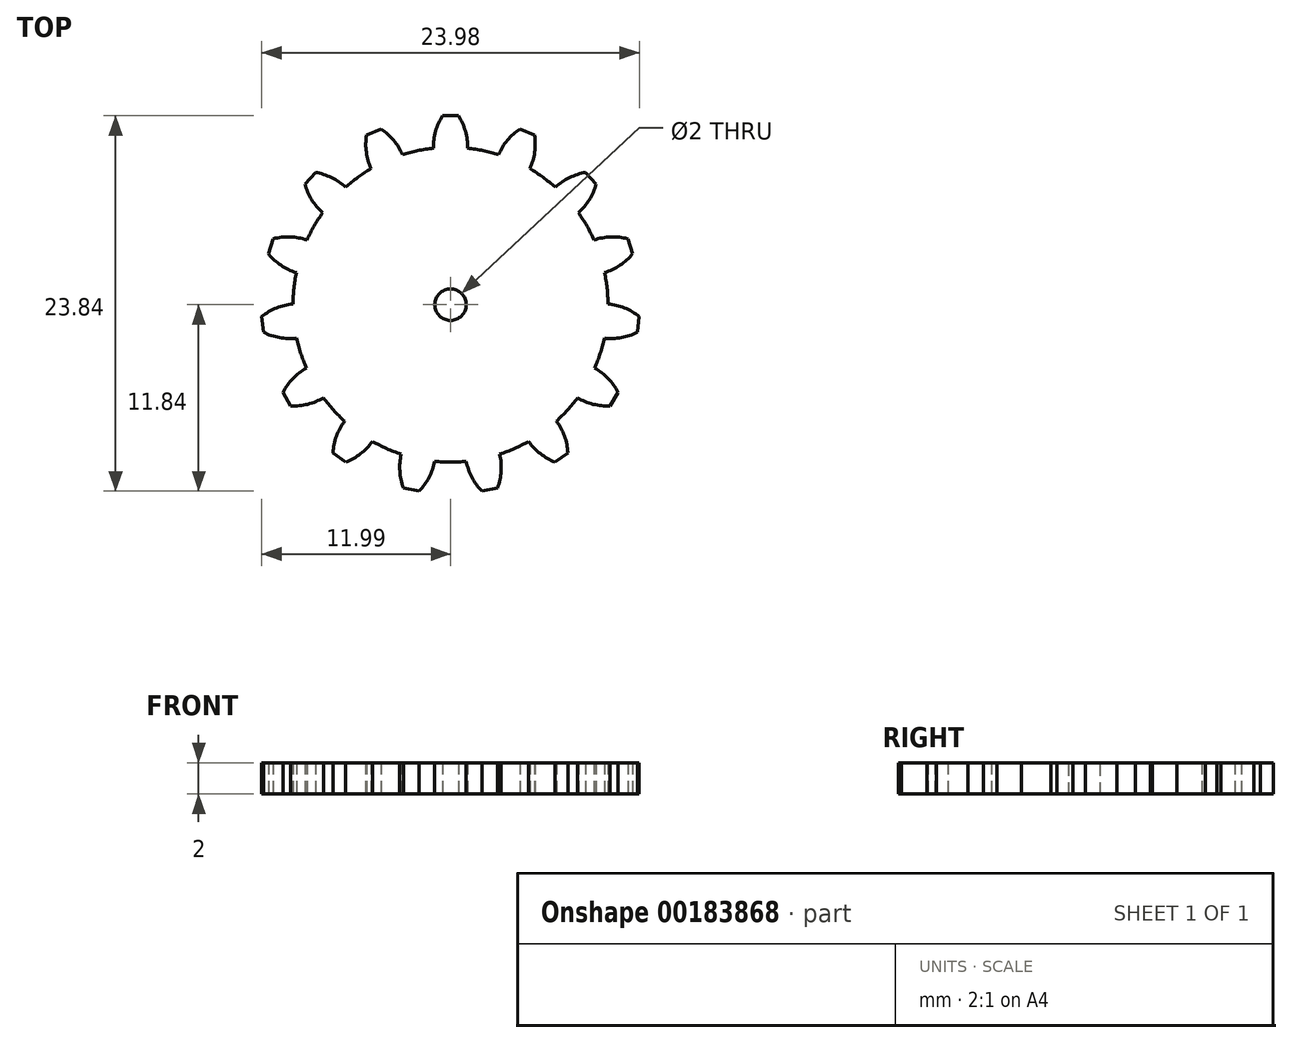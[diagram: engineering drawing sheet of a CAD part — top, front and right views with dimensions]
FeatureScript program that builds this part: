
annotation { "Feature Type Name" : "Feature", "Feature Type Description" : "" }
export const myFeature = defineFeature(function(context is Context, id is Id, definition is map)
    precondition{}
    {
        {
            var Q0;
            Q0=qCreatedBy(makeId("Top.planeOp"),FACE);
            var sketch = newSketch(context, id + "F0", { "sketchPlane" : qUnion([Q0])});
            skCircle(sketch, "E0", {"center": v(0, 0) * mm, "radius": 10 * mm});
            skLineSegment(sketch, "E1", {"start": v(0, 0) * mm, "end": v(0, 10) * mm, "construction": true});
            skLineSegment(sketch, "E2", {"start": v(0, 12) * mm, "end": v(-0.5, 12) * mm});
            skArc(sketch, "E3", {"start": v(-0.5, 12) * mm, "mid": v(-0.95, 11.01) * mm, "end": v(-1.09, 9.94) * mm});
            skLineSegment(sketch, "E4.MirrorCS", {"start": v(0, 12) * mm, "end": v(0.5, 12) * mm});
            skArc(sketch, "E5.MirrorCS", {"start": v(0.5, 12) * mm, "mid": v(0.95, 11.01) * mm, "end": v(1.09, 9.94) * mm});
            skArc(sketch, "E6.1.0", {"start": v(-5.34, 10.76) * mm, "mid": v(-5.34, 9.68) * mm, "end": v(-5.04, 8.64) * mm});
            skLineSegment(sketch, "E6.1.1", {"start": v(-4.88, 10.96) * mm, "end": v(-5.34, 10.76) * mm});
            skLineSegment(sketch, "E6.1.2", {"start": v(-4.88, 10.96) * mm, "end": v(-4.42, 11.17) * mm});
            skArc(sketch, "E6.1.3", {"start": v(-4.42, 11.17) * mm, "mid": v(-3.61, 10.45) * mm, "end": v(-3.05, 9.52) * mm});
            skArc(sketch, "E6.2.0", {"start": v(-9.25, 7.66) * mm, "mid": v(-8.82, 6.67) * mm, "end": v(-8.12, 5.84) * mm});
            skLineSegment(sketch, "E6.2.1", {"start": v(-8.92, 8.03) * mm, "end": v(-9.25, 7.66) * mm});
            skLineSegment(sketch, "E6.2.2", {"start": v(-8.92, 8.03) * mm, "end": v(-8.58, 8.4) * mm});
            skArc(sketch, "E6.2.3", {"start": v(-8.58, 8.4) * mm, "mid": v(-7.55, 8.07) * mm, "end": v(-6.66, 7.46) * mm});
            skArc(sketch, "E6.3.0", {"start": v(-11.57, 3.23) * mm, "mid": v(-10.77, 2.5) * mm, "end": v(-9.8, 2.04) * mm});
            skLineSegment(sketch, "E6.3.1", {"start": v(-11.41, 3.7) * mm, "end": v(-11.57, 3.23) * mm});
            skLineSegment(sketch, "E6.3.2", {"start": v(-11.41, 3.7) * mm, "end": v(-11.26, 4.18) * mm});
            skArc(sketch, "E6.3.3", {"start": v(-11.26, 4.18) * mm, "mid": v(-10.18, 4.3) * mm, "end": v(-9.12, 4.1) * mm});
            skArc(sketch, "E6.4.0", {"start": v(-11.88, -1.75) * mm, "mid": v(-10.85, -2.1) * mm, "end": v(-9.77, -2.12) * mm});
            skLineSegment(sketch, "E6.4.1", {"start": v(-11.93, -1.25) * mm, "end": v(-11.88, -1.75) * mm});
            skLineSegment(sketch, "E6.4.2", {"start": v(-11.93, -1.25) * mm, "end": v(-11.99, -0.76) * mm});
            skArc(sketch, "E6.4.3", {"start": v(-11.99, -0.76) * mm, "mid": v(-11.05, -0.2) * mm, "end": v(-10, 0.04) * mm});
            skArc(sketch, "E6.5.0", {"start": v(-10.14, -6.43) * mm, "mid": v(-9.06, -6.33) * mm, "end": v(-8.06, -5.91) * mm});
            skLineSegment(sketch, "E6.5.1", {"start": v(-10.4, -6) * mm, "end": v(-10.14, -6.43) * mm});
            skLineSegment(sketch, "E6.5.2", {"start": v(-10.4, -6) * mm, "end": v(-10.64, -5.57) * mm});
            skArc(sketch, "E6.5.3", {"start": v(-10.64, -5.57) * mm, "mid": v(-10.01, -4.69) * mm, "end": v(-9.15, -4.03) * mm});
            skArc(sketch, "E6.6.0", {"start": v(-6.65, -10) * mm, "mid": v(-5.7, -9.47) * mm, "end": v(-4.96, -8.68) * mm});
            skLineSegment(sketch, "E6.6.1", {"start": v(-7.05, -9.7) * mm, "end": v(-6.65, -10) * mm});
            skLineSegment(sketch, "E6.6.2", {"start": v(-7.05, -9.7) * mm, "end": v(-7.46, -9.41) * mm});
            skArc(sketch, "E6.6.3", {"start": v(-7.46, -9.41) * mm, "mid": v(-7.24, -8.35) * mm, "end": v(-6.72, -7.4) * mm});
            skArc(sketch, "E6.7.0", {"start": v(-2, -11.84) * mm, "mid": v(-1.36, -10.97) * mm, "end": v(-1, -9.95) * mm});
            skLineSegment(sketch, "E6.7.1", {"start": v(-2.5, -11.74) * mm, "end": v(-2, -11.84) * mm});
            skLineSegment(sketch, "E6.7.2", {"start": v(-2.5, -11.74) * mm, "end": v(-2.98, -11.63) * mm});
            skArc(sketch, "E6.7.3", {"start": v(-2.98, -11.63) * mm, "mid": v(-3.22, -10.58) * mm, "end": v(-3.13, -9.5) * mm});
            skArc(sketch, "E6.8.0", {"start": v(2.98, -11.63) * mm, "mid": v(3.22, -10.58) * mm, "end": v(3.13, -9.5) * mm});
            skLineSegment(sketch, "E6.8.1", {"start": v(2.5, -11.74) * mm, "end": v(2.98, -11.63) * mm});
            skLineSegment(sketch, "E6.8.2", {"start": v(2.5, -11.74) * mm, "end": v(2, -11.84) * mm});
            skArc(sketch, "E6.8.3", {"start": v(2, -11.84) * mm, "mid": v(1.36, -10.97) * mm, "end": v(1, -9.95) * mm});
            skArc(sketch, "E6.9.0", {"start": v(7.46, -9.41) * mm, "mid": v(7.24, -8.35) * mm, "end": v(6.72, -7.4) * mm});
            skLineSegment(sketch, "E6.9.1", {"start": v(7.05, -9.7) * mm, "end": v(7.46, -9.41) * mm});
            skLineSegment(sketch, "E6.9.2", {"start": v(7.05, -9.7) * mm, "end": v(6.65, -10) * mm});
            skArc(sketch, "E6.9.3", {"start": v(6.65, -10) * mm, "mid": v(5.7, -9.47) * mm, "end": v(4.96, -8.68) * mm});
            skArc(sketch, "E6.10.0", {"start": v(10.64, -5.57) * mm, "mid": v(10.01, -4.69) * mm, "end": v(9.15, -4.03) * mm});
            skLineSegment(sketch, "E6.10.1", {"start": v(10.4, -6) * mm, "end": v(10.64, -5.57) * mm});
            skLineSegment(sketch, "E6.10.2", {"start": v(10.4, -6) * mm, "end": v(10.14, -6.43) * mm});
            skArc(sketch, "E6.10.3", {"start": v(10.14, -6.43) * mm, "mid": v(9.06, -6.33) * mm, "end": v(8.06, -5.91) * mm});
            skArc(sketch, "E6.11.0", {"start": v(11.99, -0.76) * mm, "mid": v(11.05, -0.2) * mm, "end": v(10, 0.04) * mm});
            skLineSegment(sketch, "E6.11.1", {"start": v(11.93, -1.25) * mm, "end": v(11.99, -0.76) * mm});
            skLineSegment(sketch, "E6.11.2", {"start": v(11.93, -1.25) * mm, "end": v(11.88, -1.75) * mm});
            skArc(sketch, "E6.11.3", {"start": v(11.88, -1.75) * mm, "mid": v(10.85, -2.1) * mm, "end": v(9.77, -2.12) * mm});
            skArc(sketch, "E6.12.0", {"start": v(11.26, 4.18) * mm, "mid": v(10.18, 4.3) * mm, "end": v(9.12, 4.1) * mm});
            skLineSegment(sketch, "E6.12.1", {"start": v(11.41, 3.7) * mm, "end": v(11.26, 4.18) * mm});
            skLineSegment(sketch, "E6.12.2", {"start": v(11.41, 3.7) * mm, "end": v(11.57, 3.23) * mm});
            skArc(sketch, "E6.12.3", {"start": v(11.57, 3.23) * mm, "mid": v(10.77, 2.5) * mm, "end": v(9.8, 2.04) * mm});
            skArc(sketch, "E6.13.0", {"start": v(8.58, 8.4) * mm, "mid": v(7.55, 8.07) * mm, "end": v(6.66, 7.46) * mm});
            skLineSegment(sketch, "E6.13.1", {"start": v(8.92, 8.03) * mm, "end": v(8.58, 8.4) * mm});
            skLineSegment(sketch, "E6.13.2", {"start": v(8.92, 8.03) * mm, "end": v(9.25, 7.66) * mm});
            skArc(sketch, "E6.13.3", {"start": v(9.25, 7.66) * mm, "mid": v(8.82, 6.67) * mm, "end": v(8.12, 5.84) * mm});
            skArc(sketch, "E6.14.0", {"start": v(4.42, 11.17) * mm, "mid": v(3.61, 10.45) * mm, "end": v(3.05, 9.52) * mm});
            skLineSegment(sketch, "E6.14.1", {"start": v(4.88, 10.96) * mm, "end": v(4.42, 11.17) * mm});
            skLineSegment(sketch, "E6.14.2", {"start": v(4.88, 10.96) * mm, "end": v(5.34, 10.76) * mm});
            skArc(sketch, "E6.14.3", {"start": v(5.34, 10.76) * mm, "mid": v(5.34, 9.68) * mm, "end": v(5.04, 8.64) * mm});
            skSolve(sketch);
        }
        {
            var Q0;
            Q0 = qSketchRegion(id + "F0", true);
            extrude(context, id + "F1", {"entities" : qUnion([Q0]), "depth" : 2 * mm});
        }
        {
            var Q0;
            Q0=makeQuery(id+"F1.opExtrude","CAP_FACE",FACE,{"disambiguationData":[OSD([sQuery(id+"F0.wireOp",EDGE,"E0"),sQuery(id+"F0.wireOp",EDGE,"E2"),sQuery(id+"F0.wireOp",EDGE,"E3"),sQuery(id+"F0.wireOp",EDGE,"E4.MirrorCS"),sQuery(id+"F0.wireOp",EDGE,"E5.MirrorCS"),sQuery(id+"F0.wireOp",EDGE,"E6.1.0"),sQuery(id+"F0.wireOp",EDGE,"E6.1.1"),sQuery(id+"F0.wireOp",EDGE,"E6.1.2"),sQuery(id+"F0.wireOp",EDGE,"E6.1.3"),sQuery(id+"F0.wireOp",EDGE,"E6.2.0"),sQuery(id+"F0.wireOp",EDGE,"E6.2.1"),sQuery(id+"F0.wireOp",EDGE,"E6.2.2"),sQuery(id+"F0.wireOp",EDGE,"E6.2.3"),sQuery(id+"F0.wireOp",EDGE,"E6.3.0"),sQuery(id+"F0.wireOp",EDGE,"E6.3.1"),sQuery(id+"F0.wireOp",EDGE,"E6.3.2"),sQuery(id+"F0.wireOp",EDGE,"E6.3.3"),sQuery(id+"F0.wireOp",EDGE,"E6.4.0"),sQuery(id+"F0.wireOp",EDGE,"E6.4.1"),sQuery(id+"F0.wireOp",EDGE,"E6.4.2"),sQuery(id+"F0.wireOp",EDGE,"E6.4.3"),sQuery(id+"F0.wireOp",EDGE,"E6.5.0"),sQuery(id+"F0.wireOp",EDGE,"E6.5.1"),sQuery(id+"F0.wireOp",EDGE,"E6.5.2"),sQuery(id+"F0.wireOp",EDGE,"E6.5.3"),sQuery(id+"F0.wireOp",EDGE,"E6.6.0"),sQuery(id+"F0.wireOp",EDGE,"E6.6.1"),sQuery(id+"F0.wireOp",EDGE,"E6.6.2"),sQuery(id+"F0.wireOp",EDGE,"E6.6.3"),sQuery(id+"F0.wireOp",EDGE,"E6.7.0"),sQuery(id+"F0.wireOp",EDGE,"E6.7.1"),sQuery(id+"F0.wireOp",EDGE,"E6.7.2"),sQuery(id+"F0.wireOp",EDGE,"E6.7.3"),sQuery(id+"F0.wireOp",EDGE,"E6.8.0"),sQuery(id+"F0.wireOp",EDGE,"E6.8.1"),sQuery(id+"F0.wireOp",EDGE,"E6.8.2"),sQuery(id+"F0.wireOp",EDGE,"E6.8.3"),sQuery(id+"F0.wireOp",EDGE,"E6.9.0"),sQuery(id+"F0.wireOp",EDGE,"E6.9.1"),sQuery(id+"F0.wireOp",EDGE,"E6.9.2"),sQuery(id+"F0.wireOp",EDGE,"E6.9.3"),sQuery(id+"F0.wireOp",EDGE,"E6.10.0"),sQuery(id+"F0.wireOp",EDGE,"E6.10.1"),sQuery(id+"F0.wireOp",EDGE,"E6.10.2"),sQuery(id+"F0.wireOp",EDGE,"E6.10.3"),sQuery(id+"F0.wireOp",EDGE,"E6.11.0"),sQuery(id+"F0.wireOp",EDGE,"E6.11.1"),sQuery(id+"F0.wireOp",EDGE,"E6.11.2"),sQuery(id+"F0.wireOp",EDGE,"E6.11.3"),sQuery(id+"F0.wireOp",EDGE,"E6.12.0"),sQuery(id+"F0.wireOp",EDGE,"E6.12.1"),sQuery(id+"F0.wireOp",EDGE,"E6.12.2"),sQuery(id+"F0.wireOp",EDGE,"E6.12.3"),sQuery(id+"F0.wireOp",EDGE,"E6.13.0"),sQuery(id+"F0.wireOp",EDGE,"E6.13.1"),sQuery(id+"F0.wireOp",EDGE,"E6.13.2"),sQuery(id+"F0.wireOp",EDGE,"E6.13.3"),sQuery(id+"F0.wireOp",EDGE,"E6.14.0"),sQuery(id+"F0.wireOp",EDGE,"E6.14.1"),sQuery(id+"F0.wireOp",EDGE,"E6.14.2"),sQuery(id+"F0.wireOp",EDGE,"E6.14.3")])],"isStart":false});
            var sketch = newSketch(context, id + "F2", { "sketchPlane" : qUnion([Q0])});
            skCircle(sketch, "E7", {"center": v(0, 0) * mm, "radius": 1 * mm});
            skSolve(sketch);
        }
        {
            var Q0;
            Q0=makeQuery(id+"F2.imprint","IMPRINT",FACE,{"disambiguationData":[TD([[makeQuery(id+"F2.imprint","IMPRINT",EDGE,{"derivedFrom":sQuery(id+"F2.wireOp",EDGE,"E7")}),1.0]])]});
            extrude(context, id + "F3", {"entities" : qUnion([Q0]), "operationType" : NewBodyOperationType.REMOVE, "endBound" : BoundingType.THROUGH_ALL, "oppositeDirection" : true, "depth" : 25 * mm});
        }
    });
